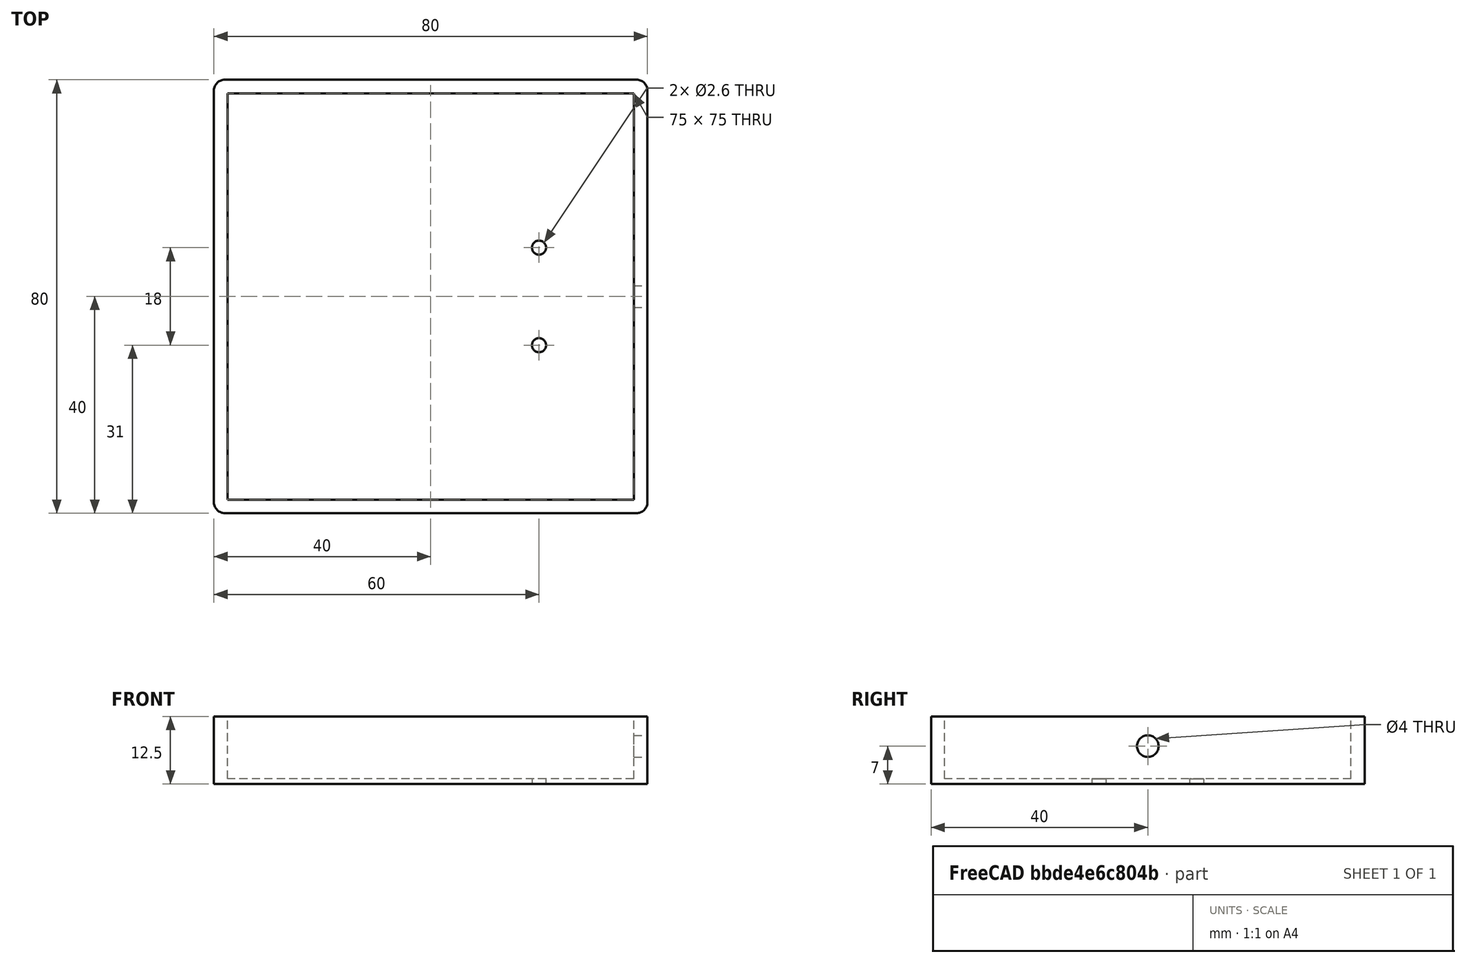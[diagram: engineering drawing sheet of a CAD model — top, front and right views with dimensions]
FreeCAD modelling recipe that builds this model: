
FCSTD DOCUMENT  (FreeCAD 0.18R16117 (Git))
Label: solar_wanne_v2
License: All rights reserved
LicenseURL: http://en.wikipedia.org/wiki/All_rights_reserved
objects: TechDraw::DrawViewDimension×9, Sketcher::SketchObject×2, Part::Extrusion×2, TechDraw::DrawProjGroupItem×2, Part::Cylinder×1, Part::MultiFuse×1, Part::Cut×1, TechDraw::DrawSVGTemplate×1, TechDraw::DrawProjGroup×1, TechDraw::DrawPage×1
note: 7 computed .brp shape members not serialized (recipe doc carries the construction recipe); baked Part::Feature solids carry a one-line shape summary decoded from their .brp

FEATURE [Sketcher::SketchObject] Sketch004  label="Sketch_solar_rahmen"
  sketch-geometry (12):
    g0: LineSegment StartX=-38 StartY=40 StartZ=0 EndX=38 EndY=40 EndZ=0
    g1: LineSegment StartX=40 StartY=38 StartZ=0 EndX=40 EndY=-38 EndZ=0
    g2: LineSegment StartX=38 StartY=-40 StartZ=0 EndX=-38 EndY=-40 EndZ=0
    g3: LineSegment StartX=-40 StartY=-38 StartZ=0 EndX=-40 EndY=38 EndZ=0
    g4: LineSegment StartX=-37.5 StartY=-37.5 StartZ=0 EndX=37.5 EndY=-37.5 EndZ=0
    g5: LineSegment StartX=37.5 StartY=-37.5 StartZ=0 EndX=37.5 EndY=37.5 EndZ=0
    g6: LineSegment StartX=37.5 StartY=37.5 StartZ=0 EndX=-37.5 EndY=37.5 EndZ=0
    g7: LineSegment StartX=-37.5 StartY=37.5 StartZ=0 EndX=-37.5 EndY=-37.5 EndZ=0
    g8: ArcOfCircle CenterX=-38 CenterY=38 CenterZ=0 NormalX=0 NormalY=0 NormalZ=1 AngleXU=0 Radius=2 StartAngle=1.5708 EndAngle=3.14159
    g9: ArcOfCircle CenterX=38 CenterY=38 CenterZ=0 NormalX=0 NormalY=0 NormalZ=1 AngleXU=0 Radius=2 StartAngle=9e-16 EndAngle=1.5708
    g10: ArcOfCircle CenterX=-38 CenterY=-38 CenterZ=0 NormalX=0 NormalY=0 NormalZ=1 AngleXU=0 Radius=2 StartAngle=3.14159 EndAngle=4.71239
    g11: ArcOfCircle CenterX=38 CenterY=-38 CenterZ=0 NormalX=0 NormalY=0 NormalZ=1 AngleXU=0 Radius=2 StartAngle=4.71239 EndAngle=6.28319
  constraints (28):
    c: Horizontal(g0)
    c: Horizontal(g2)
    c: Vertical(g1)
    c: Vertical(g3)
    c: Coincident(g4,g5)
    c: Coincident(g5,g6)
    c: Coincident(g6,g7)
    c: Coincident(g7,g4)
    c: Horizontal(g6)
    c: Vertical(g7)
    c: DistanceX(g4,g4) = 75
    c: DistanceY(g5,g5) = 75
    c: Tangent(g3,g8) = 1.5708
    c: Tangent(g0,g8) = 1.5708
    c: Tangent(g0,g9) = 1.5708
    c: Tangent(g1,g9) = 1.5708
    c: Tangent(g3,g10) = 1.5708
    c: Tangent(g2,g10) = 1.5708
    c: Tangent(g2,g11) = 1.5708
    c: Tangent(g1,g11) = 1.5708
    c: Radius(g8) = 2
    c: Equal(g8,g9)
    c: DistanceY(g2,g0) = 80
    c: DistanceX(g3,g1) = 80
    c: Symmetric(g0,g2,g-1)
    c: Symmetric(g3,g1,g-2)
    c: Symmetric(g4,g4,g-2)
    c: Symmetric(g4,g5,g-1)
FEATURE [Part::Extrusion] Extrude004  label="solar_rahmen_roh"
  Base = -> Sketch004
  Dir = (0,0,1)
  DirMode = 2
  FaceMakerClass = Part::FaceMakerBullseye
  LengthFwd = 12.5
  LengthRev = 0
  Solid = true
  Symmetric = false
FEATURE [Part::Cylinder] Cylinder001  label="bohrung_solar_wanne"
  Angle = 360
  AttacherType = Attacher::AttachEngine3D
  Height = 10
  Placement = pos=(35,0,7) rot=(0,1,0;1.5708rad)
  Radius = 2
FEATURE [Sketcher::SketchObject] Sketch005  label="Sketch_solar_rahmen_boden"
  ExternalGeometry = -> [Extrude004]
  sketch-geometry (6):
    g0: LineSegment StartX=-37.5 StartY=37.5 StartZ=0 EndX=37.5 EndY=37.5 EndZ=0
    g1: LineSegment StartX=37.5 StartY=37.5 StartZ=0 EndX=37.5 EndY=-37.5 EndZ=0
    g2: LineSegment StartX=37.5 StartY=-37.5 StartZ=0 EndX=-37.5 EndY=-37.5 EndZ=0
    g3: LineSegment StartX=-37.5 StartY=-37.5 StartZ=0 EndX=-37.5 EndY=37.5 EndZ=0
    g4: Circle CenterX=20 CenterY=9 CenterZ=0 NormalX=0 NormalY=0 NormalZ=1 AngleXU=0 Radius=1.3
    g5: Circle CenterX=20 CenterY=-9 CenterZ=0 NormalX=0 NormalY=0 NormalZ=1 AngleXU=0 Radius=1.3
  constraints (15):
    c: Coincident(g0,g1)
    c: Coincident(g1,g2)
    c: Coincident(g2,g3)
    c: Coincident(g3,g0)
    c: Horizontal(g0)
    c: Horizontal(g2)
    c: Vertical(g1)
    c: Vertical(g3)
    c: Coincident(g0,g-4)
    c: Coincident(g1,g-6)
    c: Radius(g4) = 1.3
    c: Equal(g4,g5)
    c: Symmetric(g4,g5,g-1)
    c: DistanceY(g5,g4) = 18
    c: DistanceX(g-1,g5) = 20
FEATURE [Part::Extrusion] Extrude005  label="solar_rahmen_boden"
  Base = -> Sketch005
  Dir = (0,0,1)
  DirMode = 2
  FaceMakerClass = Part::FaceMakerBullseye
  LengthFwd = 1
  LengthRev = 0
  Solid = true
  Symmetric = false
FEATURE [Part::MultiFuse] Fusion002  label="solar_wanne_ohne_bohrung"
  Shapes = -> [Extrude004,Extrude005]
FEATURE [Part::Cut] Cut001  label="solar_wanne"
  Base = -> Fusion002
  Tool = -> Cylinder001
FEATURE [TechDraw::DrawSVGTemplate] Template
  EditableTexts = Designed_by_Name=W.Klenner; FC-Date=4.3.2020; FC-SC=1:1; FC-SH=1; FC-Title=Energy Harvester; Subtitle=Solarmodul Wanne
  Height = 210
  Orientation = 1
  Width = 297
FEATURE [TechDraw::DrawProjGroupItem] ProjItem  label="Front"
  CoarseView = false
  Direction = (0,0,1)
  Focus = 100
  HardHidden = false
  IsoCount = 0
  IsoHidden = false
  IsoVisible = false
  LockPosition = true
  Perspective = false
  Rotation = 0
  RotationVector = (1,0,0)
  ScaleType = 2
  SeamHidden = false
  SeamVisible = false
  SmoothHidden = false
  SmoothVisible = false
  Source = -> [Cut001]
  Type = 0
  X = 0
  Y = 0
FEATURE [TechDraw::DrawProjGroupItem] ProjItem001  label="Right"
  CoarseView = false
  Direction = (1,0,1e-16)
  Focus = 100
  HardHidden = true
  IsoCount = 0
  IsoHidden = false
  IsoVisible = false
  LockPosition = false
  Perspective = false
  Rotation = 0
  RotationVector = (1e-16,0,-1)
  ScaleType = 2
  SeamHidden = false
  SeamVisible = false
  SmoothHidden = true
  SmoothVisible = false
  Source = -> [Cut001]
  Type = 2
  X = -95
  Y = 0
FEATURE [TechDraw::DrawProjGroup] ProjGroup
  Anchor = -> ProjItem
  AutoDistribute = true
  LockPosition = false
  ProjectionType = 0
  Rotation = 0
  ScaleType = 0
  Source = -> [Cut001]
  Views = -> [ProjItem,ProjItem001]
  X = 180.808
  Y = 138.61
  spacingX = 15
  spacingY = 15
FEATURE [TechDraw::DrawViewDimension] Dimension
  Arbitrary = false
  FormatSpec = %.2f
  LockPosition = false
  MeasureType = 1
  OverTolerance = 0
  References2D = -> [ProjItem]
  Rotation = 0
  ScaleType = 0
  Type = 1
  UnderTolerance = 0
  X = 0.150779
  Y = -53.0302
FEATURE [TechDraw::DrawViewDimension] Dimension001
  Arbitrary = false
  FormatSpec = %.2f
  LockPosition = false
  MeasureType = 1
  OverTolerance = 0
  References2D = -> [ProjItem]
  Rotation = 0
  ScaleType = 0
  Type = 1
  UnderTolerance = 0
  X = 3.56767
  Y = -64.5111
FEATURE [TechDraw::DrawViewDimension] Dimension002
  Arbitrary = false
  FormatSpec = %.2f
  LockPosition = false
  MeasureType = 1
  OverTolerance = 0
  References2D = -> [ProjItem]
  Rotation = 0
  ScaleType = 0
  Type = 2
  UnderTolerance = 0
  X = -52.2464
  Y = -2.85414
FEATURE [TechDraw::DrawViewDimension] Dimension003
  Arbitrary = false
  FormatSpec = %.2f
  LockPosition = false
  MeasureType = 1
  OverTolerance = 0
  References2D = -> [ProjItem]
  Rotation = 0
  ScaleType = 0
  Type = 2
  UnderTolerance = 0
  X = -64.0354
  Y = -3.09198
FEATURE [TechDraw::DrawViewDimension] Dimension004
  Arbitrary = false
  FormatSpec = %.2f
  LockPosition = false
  MeasureType = 1
  OverTolerance = 0
  References2D = -> [ProjItem]
  Rotation = 0
  ScaleType = 0
  Type = 2
  UnderTolerance = 0
  X = 24.6248
  Y = 0.49551
FEATURE [TechDraw::DrawViewDimension] Dimension005
  Arbitrary = false
  FormatSpec = %.2f
  LockPosition = false
  MeasureType = 1
  OverTolerance = 0
  References2D = -> [ProjItem]
  Rotation = 0
  ScaleType = 0
  Type = 1
  UnderTolerance = 0
  X = 30.3303
  Y = -14.9461
FEATURE [TechDraw::DrawViewDimension] Dimension006
  Arbitrary = false
  FormatSpec = %.2f
  LockPosition = false
  MeasureType = 1
  OverTolerance = 0
  References2D = -> [ProjItem001]
  Rotation = 0
  ScaleType = 0
  Type = 1
  UnderTolerance = 0
  X = 1.58563
  Y = -53.0815
FEATURE [TechDraw::DrawViewDimension] Dimension007
  Arbitrary = false
  FormatSpec = ⌀%.2f
  LockPosition = false
  MeasureType = 1
  OverTolerance = 0
  References2D = -> [ProjItem]
  Rotation = 0
  ScaleType = 0
  Type = 5
  UnderTolerance = 0
  X = 0
  Y = 0
FEATURE [TechDraw::DrawViewDimension] Dimension008
  Arbitrary = false
  FormatSpec = ⌀%.2f
  LockPosition = false
  MeasureType = 1
  OverTolerance = 0
  References2D = -> [ProjItem001]
  Rotation = 0
  ScaleType = 0
  Type = 5
  UnderTolerance = 0
  X = 15.2617
  Y = 5.74792
FEATURE [TechDraw::DrawPage] Page
  KeepUpdated = true
  ProjectionType = 0
  Template = -> Template
  Views = -> [ProjGroup,Dimension,Dimension001,Dimension002,Dimension003,Dimension004,Dimension005,Dimension006,Dimension007,Dimension008]
